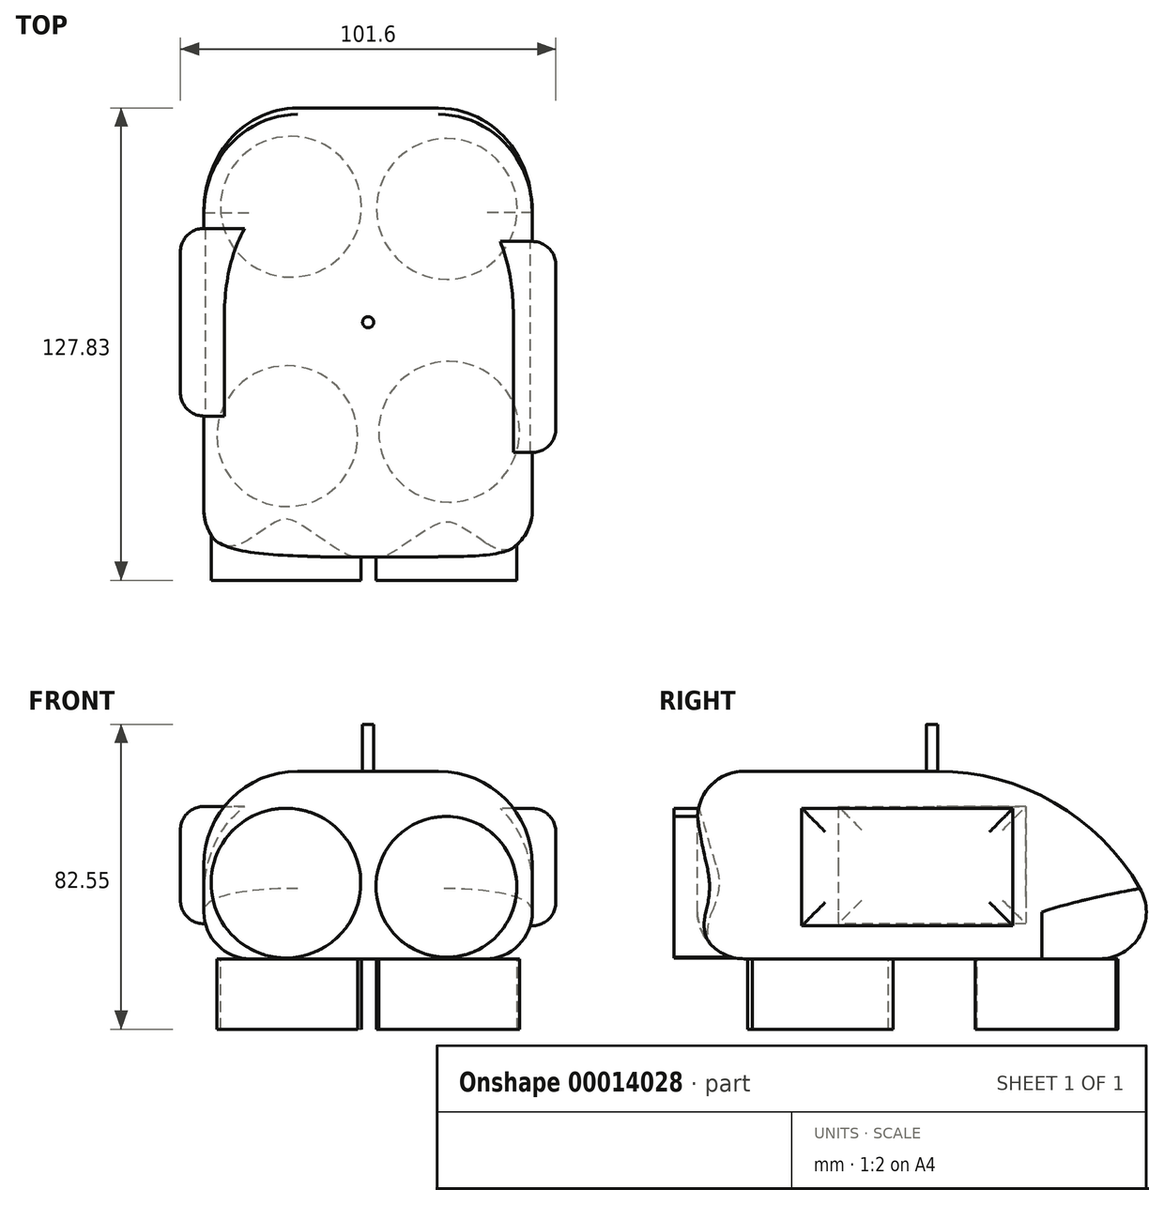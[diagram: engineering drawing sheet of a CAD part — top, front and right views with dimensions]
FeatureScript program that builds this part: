
annotation { "Feature Type Name" : "Feature", "Feature Type Description" : "" }
export const myFeature = defineFeature(function(context is Context, id is Id, definition is map)
    precondition{}
    {
        {
            var Q0;
            Q0=qCreatedBy(makeId("Top.planeOp"),FACE);
            var sketch = newSketch(context, id + "F0", { "sketchPlane" : qUnion([Q0])});
            skLineSegment(sketch, "E0.rect.bottom", {"start": v(44.45, 63.5) * mm, "end": v(-44.45, 63.5) * mm});
            skLineSegment(sketch, "E0.rect.top", {"start": v(44.45, -63.5) * mm, "end": v(-44.45, -63.5) * mm});
            skLineSegment(sketch, "E0.rect.left", {"start": v(44.45, 63.5) * mm, "end": v(44.45, -63.5) * mm});
            skLineSegment(sketch, "E0.rect.right", {"start": v(-44.45, 63.5) * mm, "end": v(-44.45, -63.5) * mm});
            skPoint(sketch, "E0.rect.middle", {"position": v(0, 0) * mm});
            skSolve(sketch);
        }
        {
            var Q0;
            Q0=makeQuery(id+"F0.imprint","IMPRINT",FACE,{"disambiguationData":[TD([[makeQuery(id+"F0.imprint","IMPRINT",EDGE,{"derivedFrom":sQuery(id+"F0.wireOp",EDGE,"E0.rect.bottom")}),1.0]])]});
            extrude(context, id + "F1", {"entities" : qUnion([Q0]), "depth" : 50.8 * mm});
        }
        {
            var Q0;
            Q0=makeQuery(id+"F1.opExtrude","CAP_EDGE",EDGE,{"disambiguationData":[OSD([sQuery(id+"F0.wireOp",EDGE,"E0.rect.bottom")])],"isStart":false});
            fillet(context, id + "F2", {"entities" : qUnion([Q0]), "radius" : 63.5 * mm, "tangentPropagation" : true, "allowEdgeOverflow" : false});
        }
        {
            var Q0;
            Q0=makeQuery(id+"F2.opFillet","BLEND_EDGE",EDGE,{"blendedFrom":[makeQuery(id+"F1.opExtrude","CAP_EDGE",EDGE,{"disambiguationData":[OSD([sQuery(id+"F0.wireOp",EDGE,"E0.rect.bottom")])],"isStart":false}),makeQuery(id+"F1.opExtrude","SWEPT_FACE",FACE,{"disambiguationData":[OSD([sQuery(id+"F0.wireOp",EDGE,"E0.rect.left")])]})],"blendedInto":[makeQuery(id+"F1.opExtrude","SWEPT_FACE",FACE,{"disambiguationData":[OSD([sQuery(id+"F0.wireOp",EDGE,"E0.rect.left")])]})]});
            var Q1;
            Q1=makeQuery(id+"F2.opFillet","BLEND_EDGE",EDGE,{"blendedFrom":[makeQuery(id+"F1.opExtrude","CAP_EDGE",EDGE,{"disambiguationData":[OSD([sQuery(id+"F0.wireOp",EDGE,"E0.rect.bottom")])],"isStart":false}),makeQuery(id+"F1.opExtrude","SWEPT_FACE",FACE,{"disambiguationData":[OSD([sQuery(id+"F0.wireOp",EDGE,"E0.rect.right")])]})],"blendedInto":[makeQuery(id+"F1.opExtrude","SWEPT_FACE",FACE,{"disambiguationData":[OSD([sQuery(id+"F0.wireOp",EDGE,"E0.rect.right")])]})]});
            var Q2;
            Q2=makeQuery(id+"F1.opExtrude","CAP_EDGE",EDGE,{"disambiguationData":[OSD([sQuery(id+"F0.wireOp",EDGE,"E0.rect.right")])],"isStart":false});
            fillet(context, id + "F3", {"entities" : qUnion([Q0, Q1, Q2]), "radius" : 25.4 * mm, "tangentPropagation" : true, "allowEdgeOverflow" : false});
        }
        {
            var Q0;
            Q0=makeQuery(id+"F3.opFillet","BLEND_EDGE",EDGE,{"blendedFrom":[makeQuery(id+"F1.opExtrude","CAP_EDGE",EDGE,{"disambiguationData":[OSD([sQuery(id+"F0.wireOp",EDGE,"E0.rect.left")])],"isStart":false}),makeQuery(id+"F1.opExtrude","SWEPT_FACE",FACE,{"disambiguationData":[OSD([sQuery(id+"F0.wireOp",EDGE,"E0.rect.top")])]})],"blendedInto":[makeQuery(id+"F1.opExtrude","SWEPT_FACE",FACE,{"disambiguationData":[OSD([sQuery(id+"F0.wireOp",EDGE,"E0.rect.top")])]})]});
            fillet(context, id + "F4", {"entities" : qUnion([Q0]), "radius" : 12.7 * mm, "tangentPropagation" : true, "allowEdgeOverflow" : false});
        }
        {
            var Q0;
            Q0=qCreatedBy(makeId("Top.planeOp"),FACE);
            var sketch = newSketch(context, id + "F5", { "sketchPlane" : qUnion([Q0])});
            skCircle(sketch, "E1", {"center": v(21.31, 30.67) * mm, "radius": 19.05 * mm});
            skCircle(sketch, "E2", {"center": v(-20.89, 31.26) * mm, "radius": 19.05 * mm});
            skCircle(sketch, "E3", {"center": v(21.91, -29.65) * mm, "radius": 19.05 * mm});
            skCircle(sketch, "E4", {"center": v(-21.88, -30.85) * mm, "radius": 19.05 * mm});
            skSolve(sketch);
        }
        {
            var Q0;
            Q0=makeQuery(id+"F5.imprint","IMPRINT",FACE,{"disambiguationData":[TD([[makeQuery(id+"F5.imprint","IMPRINT",EDGE,{"derivedFrom":sQuery(id+"F5.wireOp",EDGE,"E1")}),1.0]])]});
            var Q1;
            Q1=makeQuery(id+"F5.imprint","IMPRINT",FACE,{"disambiguationData":[TD([[makeQuery(id+"F5.imprint","IMPRINT",EDGE,{"derivedFrom":sQuery(id+"F5.wireOp",EDGE,"E2")}),1.0]])]});
            var Q2;
            Q2=makeQuery(id+"F5.imprint","IMPRINT",FACE,{"disambiguationData":[TD([[makeQuery(id+"F5.imprint","IMPRINT",EDGE,{"derivedFrom":sQuery(id+"F5.wireOp",EDGE,"E4")}),1.0]])]});
            var Q3;
            Q3=makeQuery(id+"F5.imprint","IMPRINT",FACE,{"disambiguationData":[TD([[makeQuery(id+"F5.imprint","IMPRINT",EDGE,{"derivedFrom":sQuery(id+"F5.wireOp",EDGE,"E3")}),1.0]])]});
            var Q4;
            Q4=sQuery(id+"F5.wireOp",EDGE,"E1");
            extrude(context, id + "F6", {"entities" : qUnion([Q0, Q1, Q2, Q3]), "surfaceEntities" : qUnion([Q4]), "oppositeDirection" : true, "depth" : 19.05 * mm});
        }
        {
            var Q0;
            Q0=qCreatedBy(makeId("Front.planeOp"),FACE);
            var sketch = newSketch(context, id + "F7", { "sketchPlane" : qUnion([Q0])});
            skCircle(sketch, "E5", {"center": v(-22.25, 20.5) * mm, "radius": 20.25 * mm});
            skCircle(sketch, "E6", {"center": v(21.18, 19.48) * mm, "radius": 19.05 * mm});
            skSolve(sketch);
        }
        {
            var Q0;
            Q0 = qSketchRegion(id + "F7", true);
            var Q1;
            Q1=sQuery(id+"F7.wireOp",EDGE,"E6");
            var Q2;
            Q2=sQuery(id+"F7.wireOp",EDGE,"E5");
            extrude(context, id + "F8", {"entities" : qUnion([Q0]), "surfaceEntities" : qUnion([Q1, Q2]), "depth" : 69.85 * mm});
        }
        {
            var Q0;
            {var subQ0=sQuery(id+"F0.wireOp",EDGE,"E0.rect.bottom");var subQ1=sQuery(id+"F0.wireOp",EDGE,"E0.rect.right");Q0=makeQuery(id+"F3.opFillet","BLEND_EDGE",EDGE,{"blendedFrom":[makeQuery(id+"F2.opFillet","BLEND_EDGE",EDGE,{"blendedFrom":[makeQuery(id+"F1.opExtrude","CAP_EDGE",EDGE,{"disambiguationData":[OSD([subQ0])],"isStart":false}),makeQuery(id+"F1.opExtrude","SWEPT_FACE",FACE,{"disambiguationData":[OSD([subQ1])]})],"blendedInto":[makeQuery(id+"F1.opExtrude","SWEPT_FACE",FACE,{"disambiguationData":[OSD([subQ1])]})]}),makeQuery(id+"F1.opExtrude","CAP_FACE",FACE,{"disambiguationData":[OSD([subQ0,sQuery(id+"F0.wireOp",EDGE,"E0.rect.top"),sQuery(id+"F0.wireOp",EDGE,"E0.rect.left"),subQ1])],"isStart":true})],"blendedInto":[makeQuery(id+"F1.opExtrude","CAP_FACE",FACE,{"disambiguationData":[OSD([subQ0,sQuery(id+"F0.wireOp",EDGE,"E0.rect.top"),sQuery(id+"F0.wireOp",EDGE,"E0.rect.left"),subQ1])],"isStart":true})]});}
            var Q1;
            {var subQ0=sQuery(id+"F0.wireOp",EDGE,"E0.rect.top");var subQ1=sQuery(id+"F0.wireOp",EDGE,"E0.rect.right");Q1=makeQuery(id+"F4.opFillet","BLEND_EDGE",EDGE,{"blendedFrom":[makeQuery(id+"F1.opExtrude","SWEPT_EDGE",EDGE,{"disambiguationData":[OSD([subQ0,subQ1])]}),makeQuery(id+"F1.opExtrude","CAP_FACE",FACE,{"disambiguationData":[OSD([sQuery(id+"F0.wireOp",EDGE,"E0.rect.bottom"),subQ0,sQuery(id+"F0.wireOp",EDGE,"E0.rect.left"),subQ1])],"isStart":true})],"blendedInto":[makeQuery(id+"F1.opExtrude","CAP_FACE",FACE,{"disambiguationData":[OSD([sQuery(id+"F0.wireOp",EDGE,"E0.rect.bottom"),subQ0,sQuery(id+"F0.wireOp",EDGE,"E0.rect.left"),subQ1])],"isStart":true})]});}
            var Q2;
            {var subQ0=sQuery(id+"F0.wireOp",EDGE,"E0.rect.bottom");var subQ1=sQuery(id+"F0.wireOp",EDGE,"E0.rect.left");Q2=makeQuery(id+"F3.opFillet","BLEND_EDGE",EDGE,{"blendedFrom":[makeQuery(id+"F2.opFillet","BLEND_EDGE",EDGE,{"blendedFrom":[makeQuery(id+"F1.opExtrude","CAP_EDGE",EDGE,{"disambiguationData":[OSD([subQ0])],"isStart":false}),makeQuery(id+"F1.opExtrude","SWEPT_FACE",FACE,{"disambiguationData":[OSD([subQ1])]})],"blendedInto":[makeQuery(id+"F1.opExtrude","SWEPT_FACE",FACE,{"disambiguationData":[OSD([subQ1])]})]}),makeQuery(id+"F1.opExtrude","CAP_FACE",FACE,{"disambiguationData":[OSD([subQ0,sQuery(id+"F0.wireOp",EDGE,"E0.rect.top"),subQ1,sQuery(id+"F0.wireOp",EDGE,"E0.rect.right")])],"isStart":true})],"blendedInto":[makeQuery(id+"F1.opExtrude","CAP_FACE",FACE,{"disambiguationData":[OSD([subQ0,sQuery(id+"F0.wireOp",EDGE,"E0.rect.top"),subQ1,sQuery(id+"F0.wireOp",EDGE,"E0.rect.right")])],"isStart":true})]});}
            var Q3;
            Q3=makeQuery(id+"F1.opExtrude","CAP_EDGE",EDGE,{"disambiguationData":[OSD([sQuery(id+"F0.wireOp",EDGE,"E0.rect.left")])],"isStart":true});
            var Q4;
            Q4=makeQuery(id+"F1.opExtrude","CAP_EDGE",EDGE,{"disambiguationData":[OSD([sQuery(id+"F0.wireOp",EDGE,"E0.rect.right")])],"isStart":true});
            var Q5;
            Q5=makeQuery(id+"F1.opExtrude","CAP_EDGE",EDGE,{"disambiguationData":[OSD([sQuery(id+"F0.wireOp",EDGE,"E0.rect.top")])],"isStart":true});
            var Q6;
            {var subQ0=sQuery(id+"F0.wireOp",EDGE,"E0.rect.top");var subQ1=sQuery(id+"F0.wireOp",EDGE,"E0.rect.left");Q6=makeQuery(id+"F4.opFillet","BLEND_EDGE",EDGE,{"blendedFrom":[makeQuery(id+"F1.opExtrude","SWEPT_EDGE",EDGE,{"disambiguationData":[OSD([subQ0,subQ1])]}),makeQuery(id+"F1.opExtrude","CAP_FACE",FACE,{"disambiguationData":[OSD([sQuery(id+"F0.wireOp",EDGE,"E0.rect.bottom"),subQ0,subQ1,sQuery(id+"F0.wireOp",EDGE,"E0.rect.right")])],"isStart":true})],"blendedInto":[makeQuery(id+"F1.opExtrude","CAP_FACE",FACE,{"disambiguationData":[OSD([sQuery(id+"F0.wireOp",EDGE,"E0.rect.bottom"),subQ0,subQ1,sQuery(id+"F0.wireOp",EDGE,"E0.rect.right")])],"isStart":true})]});}
            var Q7;
            {var subQ0=sQuery(id+"F0.wireOp",EDGE,"E0.rect.bottom");Q7=makeQuery(id+"F2.opFillet","BLEND_EDGE",EDGE,{"blendedFrom":[makeQuery(id+"F1.opExtrude","CAP_EDGE",EDGE,{"disambiguationData":[OSD([subQ0])],"isStart":false}),makeQuery(id+"F1.opExtrude","CAP_FACE",FACE,{"disambiguationData":[OSD([subQ0,sQuery(id+"F0.wireOp",EDGE,"E0.rect.top"),sQuery(id+"F0.wireOp",EDGE,"E0.rect.left"),sQuery(id+"F0.wireOp",EDGE,"E0.rect.right")])],"isStart":true})],"blendedInto":[makeQuery(id+"F1.opExtrude","CAP_FACE",FACE,{"disambiguationData":[OSD([subQ0,sQuery(id+"F0.wireOp",EDGE,"E0.rect.top"),sQuery(id+"F0.wireOp",EDGE,"E0.rect.left"),sQuery(id+"F0.wireOp",EDGE,"E0.rect.right")])],"isStart":true})]});}
            fillet(context, id + "F9", {"entities" : qUnion([Q0, Q1, Q2, Q3, Q4, Q5, Q6, Q7]), "radius" : 12.7 * mm, "tangentPropagation" : true, "allowEdgeOverflow" : false});
        }
        {
            var Q0;
            Q0=qCreatedBy(makeId("Right.planeOp"),FACE);
            var sketch = newSketch(context, id + "F10", { "sketchPlane" : qUnion([Q0])});
            skLineSegment(sketch, "E7.rect.bottom", {"start": v(21.87, 40.7) * mm, "end": v(-35.28, 40.7) * mm});
            skLineSegment(sketch, "E7.rect.top", {"start": v(21.87, 8.95) * mm, "end": v(-35.28, 8.95) * mm});
            skLineSegment(sketch, "E7.rect.left", {"start": v(21.87, 40.7) * mm, "end": v(21.87, 8.95) * mm});
            skLineSegment(sketch, "E7.rect.right", {"start": v(-35.28, 40.7) * mm, "end": v(-35.28, 8.95) * mm});
            skPoint(sketch, "E7.rect.middle", {"position": v(-6.7, 24.83) * mm});
            skSolve(sketch);
        }
        {
            var Q0;
            Q0 = qSketchRegion(id + "F10", true);
            extrude(context, id + "F11", {"entities" : qUnion([Q0]), "operationType" : NewBodyOperationType.ADD, "depth" : 50.8 * mm});
        }
        {
            var Q0;
            Q0=makeQuery(id+"F11.opExtrude","CAP_EDGE",EDGE,{"disambiguationData":[OSD([sQuery(id+"F10.wireOp",EDGE,"E7.rect.bottom")])],"isStart":false});
            var Q1;
            Q1=makeQuery(id+"F11.opExtrude","CAP_EDGE",EDGE,{"disambiguationData":[OSD([sQuery(id+"F10.wireOp",EDGE,"E7.rect.top")])],"isStart":false});
            var Q2;
            Q2=makeQuery(id+"F11.opExtrude","CAP_EDGE",EDGE,{"disambiguationData":[OSD([sQuery(id+"F10.wireOp",EDGE,"E7.rect.right")])],"isStart":false});
            var Q3;
            Q3=makeQuery(id+"F11.opExtrude","CAP_EDGE",EDGE,{"disambiguationData":[OSD([sQuery(id+"F10.wireOp",EDGE,"E7.rect.left")])],"isStart":false});
            fillet(context, id + "F12", {"entities" : qUnion([Q0, Q1, Q2, Q3]), "radius" : 6.35 * mm, "tangentPropagation" : true, "allowEdgeOverflow" : false});
        }
        {
            var Q0;
            Q0=qCreatedBy(makeId("Right.planeOp"),FACE);
            var sketch = newSketch(context, id + "F13", { "sketchPlane" : qUnion([Q0])});
            skLineSegment(sketch, "E8.rect.bottom", {"start": v(-25.4, 41.23) * mm, "end": v(25.4, 41.23) * mm});
            skLineSegment(sketch, "E8.rect.top", {"start": v(-25.4, 9.48) * mm, "end": v(25.4, 9.48) * mm});
            skLineSegment(sketch, "E8.rect.left", {"start": v(-25.4, 41.23) * mm, "end": v(-25.4, 9.48) * mm});
            skLineSegment(sketch, "E8.rect.right", {"start": v(25.4, 41.23) * mm, "end": v(25.4, 9.48) * mm});
            skPoint(sketch, "E8.rect.middle", {"position": v(0, 25.36) * mm});
            skSolve(sketch);
        }
        {
            var Q0;
            Q0 = qSketchRegion(id + "F13", true);
            extrude(context, id + "F14", {"entities" : qUnion([Q0]), "operationType" : NewBodyOperationType.ADD, "oppositeDirection" : true, "depth" : 50.8 * mm});
        }
        {
            var Q0;
            Q0=makeQuery(id+"F14.opExtrude","CAP_EDGE",EDGE,{"disambiguationData":[OSD([sQuery(id+"F13.wireOp",EDGE,"E8.rect.bottom")])],"isStart":false});
            var Q1;
            Q1=makeQuery(id+"F14.opExtrude","CAP_FACE",FACE,{"disambiguationData":[OSD([sQuery(id+"F13.wireOp",EDGE,"E8.rect.bottom"),sQuery(id+"F13.wireOp",EDGE,"E8.rect.top"),sQuery(id+"F13.wireOp",EDGE,"E8.rect.left"),sQuery(id+"F13.wireOp",EDGE,"E8.rect.right")])],"isStart":false});
            var Q2;
            Q2=makeQuery(id+"F14.opExtrude","CAP_EDGE",EDGE,{"disambiguationData":[OSD([sQuery(id+"F13.wireOp",EDGE,"E8.rect.left")])],"isStart":false});
            var Q3;
            Q3=makeQuery(id+"F14.opExtrude","CAP_EDGE",EDGE,{"disambiguationData":[OSD([sQuery(id+"F13.wireOp",EDGE,"E8.rect.right")])],"isStart":false});
            fillet(context, id + "F15", {"entities" : qUnion([Q0, Q1, Q2, Q3]), "radius" : 6.35 * mm, "tangentPropagation" : true, "allowEdgeOverflow" : false});
        }
        {
            var Q0;
            Q0=qCreatedBy(makeId("Top.planeOp"),FACE);
            var sketch = newSketch(context, id + "F16", { "sketchPlane" : qUnion([Q0])});
            skCircle(sketch, "E9", {"center": v(0, 0) * mm, "radius": 1.5 * mm});
            skSolve(sketch);
        }
        {
            var Q0;
            Q0 = qSketchRegion(id + "F16", true);
            extrude(context, id + "F17", {"entities" : qUnion([Q0]), "operationType" : NewBodyOperationType.ADD, "depth" : 63.5 * mm});
        }
    });
